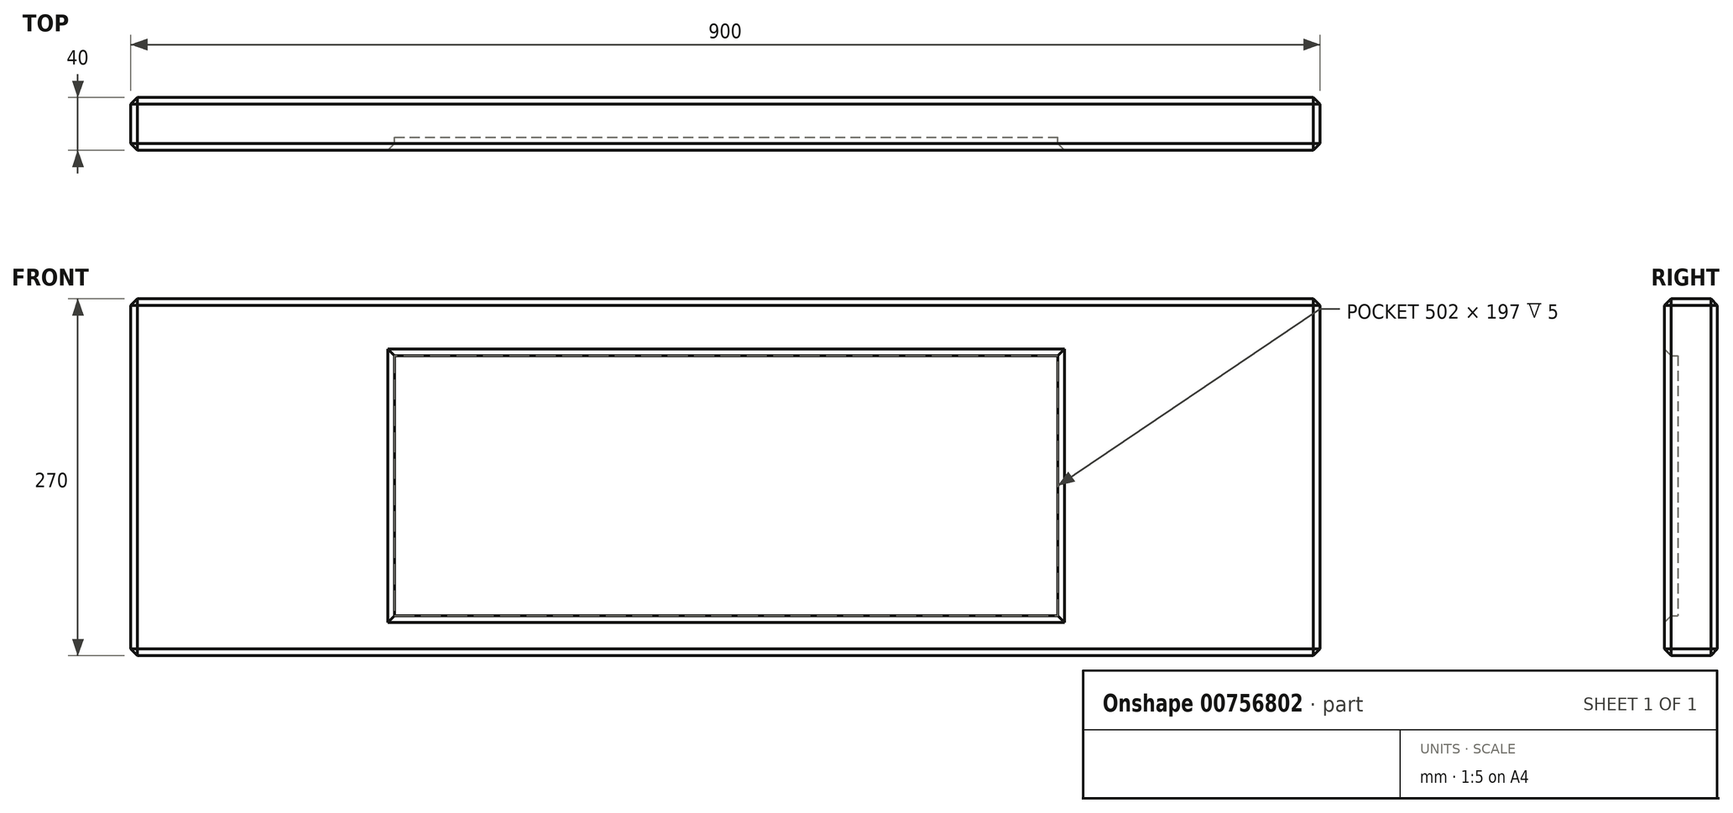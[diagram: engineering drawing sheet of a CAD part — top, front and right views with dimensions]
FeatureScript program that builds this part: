
annotation { "Feature Type Name" : "Feature", "Feature Type Description" : "" }
export const myFeature = defineFeature(function(context is Context, id is Id, definition is map)
    precondition{}
    {
        {
            var Q0;
            Q0=qCreatedBy(makeId("Front.planeOp"),FACE);
            var sketch = newSketch(context, id + "F0", { "sketchPlane" : qUnion([Q0])});
            skLineSegment(sketch, "E0.bottom", {"start": v(-464.22, 83.96) * mm, "end": v(435.78, 83.96) * mm});
            skLineSegment(sketch, "E0.top", {"start": v(-464.22, -186.04) * mm, "end": v(435.78, -186.04) * mm});
            skLineSegment(sketch, "E0.left", {"start": v(-464.22, 83.96) * mm, "end": v(-464.22, -186.04) * mm});
            skLineSegment(sketch, "E0.right", {"start": v(435.78, 83.96) * mm, "end": v(435.78, -186.04) * mm});
            skLineSegment(sketch, "E1.bottom", {"start": v(-264.59, 40.96) * mm, "end": v(237.41, 40.96) * mm});
            skLineSegment(sketch, "E1.top", {"start": v(-264.59, -156.04) * mm, "end": v(237.41, -156.04) * mm});
            skLineSegment(sketch, "E1.left", {"start": v(-264.59, 40.96) * mm, "end": v(-264.59, -156.04) * mm});
            skLineSegment(sketch, "E1.right", {"start": v(237.41, 40.96) * mm, "end": v(237.41, -156.04) * mm});
            skSolve(sketch);
        }
        {
            var Q0;
            Q0=makeQuery(id+"F0.imprint","IMPRINT",FACE,{"disambiguationData":[TD([[makeQuery(id+"F0.imprint","IMPRINT",EDGE,{"derivedFrom":sQuery(id+"F0.wireOp",EDGE,"E0.bottom")}),-1.0]])]});
            extrude(context, id + "F1", {"entities" : qUnion([Q0]), "depth" : 40 * mm, "offsetDistance" : 25 * mm});
        }
        {
            var Q0;
            Q0=makeQuery(id+"F0.imprint","IMPRINT",FACE,{"disambiguationData":[TD([[makeQuery(id+"F0.imprint","IMPRINT",EDGE,{"derivedFrom":sQuery(id+"F0.wireOp",EDGE,"E1.bottom")}),-1.0]])]});
            extrude(context, id + "F2", {"entities" : qUnion([Q0]), "operationType" : NewBodyOperationType.ADD, "depth" : 30 * mm, "offsetDistance" : 25 * mm});
        }
        {
            var Q0;
            Q0=makeQuery(id+"F1.opExtrude","CAP_FACE",FACE,{"disambiguationData":[OSD([sQuery(id+"F0.wireOp",EDGE,"E0.bottom"),sQuery(id+"F0.wireOp",EDGE,"E0.top"),sQuery(id+"F0.wireOp",EDGE,"E0.left"),sQuery(id+"F0.wireOp",EDGE,"E0.right"),sQuery(id+"F0.wireOp",EDGE,"E1.bottom"),sQuery(id+"F0.wireOp",EDGE,"E1.top"),sQuery(id+"F0.wireOp",EDGE,"E1.left"),sQuery(id+"F0.wireOp",EDGE,"E1.right")])],"isStart":false});
            var Q1;
            Q1=makeQuery(id+"F1.opExtrude","SWEPT_FACE",FACE,{"disambiguationData":[OSD([sQuery(id+"F0.wireOp",EDGE,"E0.left")])]});
            var Q2;
            Q2=makeQuery(id+"F1.opExtrude","SWEPT_FACE",FACE,{"disambiguationData":[OSD([sQuery(id+"F0.wireOp",EDGE,"E0.right")])]});
            var Q3;
            Q3=makeQuery(id+"F1.opExtrude","CAP_EDGE",EDGE,{"disambiguationData":[OSD([sQuery(id+"F0.wireOp",EDGE,"E0.top")])],"isStart":true});
            var Q4;
            Q4=makeQuery(id+"F1.opExtrude","CAP_EDGE",EDGE,{"disambiguationData":[OSD([sQuery(id+"F0.wireOp",EDGE,"E0.bottom")])],"isStart":true});
            chamfer(context, id + "F3", {"entities" : qUnion([Q0, Q1, Q2, Q3, Q4]), "width" : 5 * mm, "tangentPropagation" : true});
        }
    });
